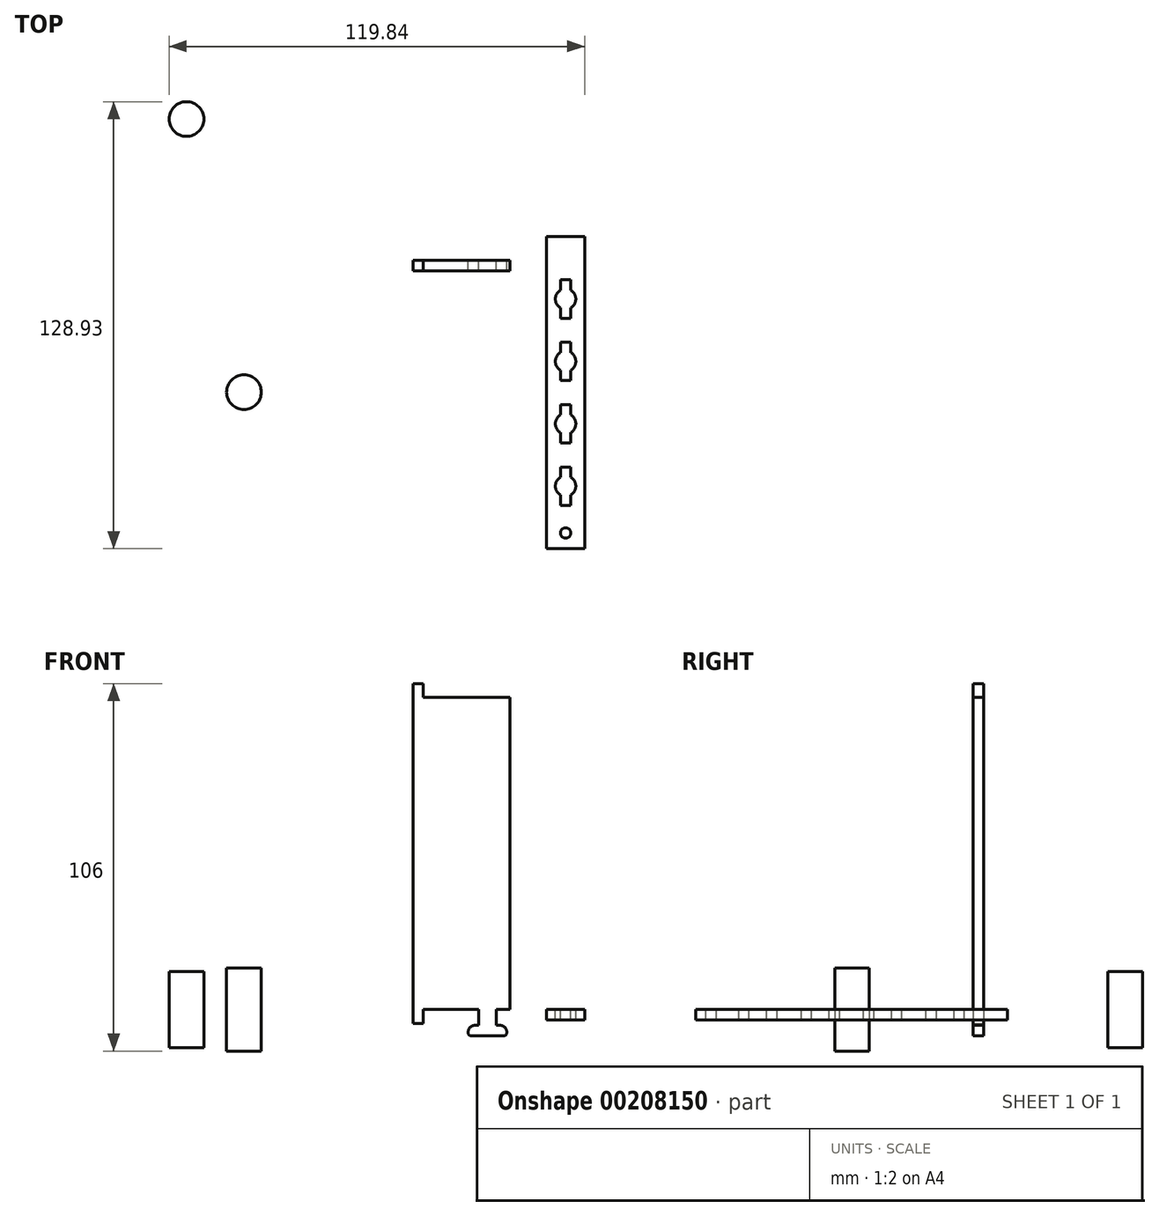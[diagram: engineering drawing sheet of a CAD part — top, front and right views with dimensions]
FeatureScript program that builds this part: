
annotation { "Feature Type Name" : "Feature", "Feature Type Description" : "" }
export const myFeature = defineFeature(function(context is Context, id is Id, definition is map)
    precondition{}
    {
        {
            var Q0;
            Q0=qCreatedBy(makeId("Front.planeOp"),FACE);
            var sketch = newSketch(context, id + "F0", { "sketchPlane" : qUnion([Q0])});
            skLineSegment(sketch, "E0.left", {"start": v(0, 0) * mm, "end": v(0, 90) * mm});
            skLineSegment(sketch, "E1.top", {"start": v(0, -4) * mm, "end": v(3, -4) * mm});
            skLineSegment(sketch, "E1.left", {"start": v(0, 0) * mm, "end": v(0, -4) * mm});
            skLineSegment(sketch, "E1.right", {"start": v(3, 0) * mm, "end": v(3, -4) * mm});
            skLineSegment(sketch, "E2.left", {"start": v(19, 0) * mm, "end": v(19, -4.6) * mm});
            skLineSegment(sketch, "E2.right", {"start": v(24, 0) * mm, "end": v(24, -4.6) * mm});
            skLineSegment(sketch, "E3.top", {"start": v(0, 94) * mm, "end": v(3, 94) * mm});
            skLineSegment(sketch, "E3.left", {"start": v(0, 90) * mm, "end": v(0, 94) * mm});
            skLineSegment(sketch, "E3.right", {"start": v(3, 90) * mm, "end": v(3, 94) * mm});
            skLineSegment(sketch, "E4", {"start": v(28, 0) * mm, "end": v(24, 0) * mm});
            skLineSegment(sketch, "E5", {"start": v(19, 0) * mm, "end": v(3, 0) * mm});
            skLineSegment(sketch, "E6", {"start": v(3, 90) * mm, "end": v(7, 90) * mm});
            skLineSegment(sketch, "E7", {"start": v(19, -4.6) * mm, "end": v(17.76, -4.6) * mm});
            skLineSegment(sketch, "E8", {"start": v(15.96, -6.4) * mm, "end": v(15.96, -6.8) * mm});
            skLineSegment(sketch, "E9", {"start": v(16.76, -7.6) * mm, "end": v(26.24, -7.6) * mm});
            skLineSegment(sketch, "E10", {"start": v(27.04, -6.8) * mm, "end": v(27.04, -6.4) * mm});
            skLineSegment(sketch, "E11", {"start": v(25.24, -4.6) * mm, "end": v(24, -4.6) * mm});
            skPoint(sketch, "E12.visualSharp", {"position": v(15.96, -4.6) * mm});
            skArc(sketch, "E12.filletArc", {"start": v(17.76, -4.6) * mm, "mid": v(16.49, -5.13) * mm, "end": v(15.96, -6.4) * mm});
            skPoint(sketch, "E13.visualSharp", {"position": v(27.04, -4.6) * mm});
            skArc(sketch, "E13.filletArc", {"start": v(27.04, -6.4) * mm, "mid": v(26.51, -5.13) * mm, "end": v(25.24, -4.6) * mm});
            skPoint(sketch, "E14.visualSharp", {"position": v(15.96, -7.6) * mm});
            skArc(sketch, "E14.filletArc", {"start": v(15.96, -6.8) * mm, "mid": v(16.2, -7.37) * mm, "end": v(16.76, -7.6) * mm});
            skPoint(sketch, "E15.visualSharp", {"position": v(27.04, -7.6) * mm});
            skArc(sketch, "E15.filletArc", {"start": v(26.24, -7.6) * mm, "mid": v(26.8, -7.37) * mm, "end": v(27.04, -6.8) * mm});
            skLineSegment(sketch, "E16", {"start": v(7, 90) * mm, "end": v(28, 90) * mm});
            skLineSegment(sketch, "E17", {"start": v(28, 0) * mm, "end": v(28, 90) * mm});
            skSolve(sketch);
        }
        {
            var Q0;
            Q0=qCreatedBy(makeId("Top.planeOp"),FACE);
            var sketch = newSketch(context, id + "F1", { "sketchPlane" : qUnion([Q0])});
            skLineSegment(sketch, "E18.bottom", {"start": v(38.53, -83.11) * mm, "end": v(49.53, -83.11) * mm});
            skLineSegment(sketch, "E18.top", {"start": v(38.53, 6.89) * mm, "end": v(49.53, 6.89) * mm});
            skLineSegment(sketch, "E18.left", {"start": v(38.53, -83.11) * mm, "end": v(38.53, 6.89) * mm});
            skLineSegment(sketch, "E18.right", {"start": v(49.53, -83.11) * mm, "end": v(49.53, 6.89) * mm});
            skLineSegment(sketch, "E19", {"start": v(44.03, 6.89) * mm, "end": v(44.03, -83.11) * mm, "construction": true});
            skCircle(sketch, "E20", {"center": v(44.03, -11.11) * mm, "radius": 2.95 * mm});
            skLineSegment(sketch, "E21", {"start": v(42.53, -8.57) * mm, "end": v(42.53, -5.57) * mm});
            skLineSegment(sketch, "E22", {"start": v(42.53, -5.57) * mm, "end": v(45.53, -5.57) * mm});
            skLineSegment(sketch, "E23", {"start": v(45.53, -5.57) * mm, "end": v(45.53, -8.57) * mm});
            skLineSegment(sketch, "E24", {"start": v(42.53, -13.65) * mm, "end": v(42.53, -16.65) * mm});
            skLineSegment(sketch, "E25", {"start": v(42.53, -16.65) * mm, "end": v(45.53, -16.65) * mm});
            skLineSegment(sketch, "E26", {"start": v(45.53, -16.65) * mm, "end": v(45.53, -13.65) * mm});
            skCircle(sketch, "E27.0.1.0", {"center": v(44.03, -29.11) * mm, "radius": 2.95 * mm});
            skLineSegment(sketch, "E27.0.1.1", {"start": v(42.53, -23.57) * mm, "end": v(45.53, -23.57) * mm});
            skLineSegment(sketch, "E27.0.1.2", {"start": v(42.53, -26.57) * mm, "end": v(42.53, -23.57) * mm});
            skLineSegment(sketch, "E27.0.1.3", {"start": v(45.53, -23.57) * mm, "end": v(45.53, -26.57) * mm});
            skLineSegment(sketch, "E27.0.1.4", {"start": v(42.53, -31.65) * mm, "end": v(42.53, -34.65) * mm});
            skLineSegment(sketch, "E27.0.1.5", {"start": v(45.53, -34.65) * mm, "end": v(45.53, -31.65) * mm});
            skLineSegment(sketch, "E27.0.1.6", {"start": v(42.53, -34.65) * mm, "end": v(45.53, -34.65) * mm});
            skCircle(sketch, "E27.0.2.0", {"center": v(44.03, -47.11) * mm, "radius": 2.95 * mm});
            skLineSegment(sketch, "E27.0.2.1", {"start": v(42.53, -41.57) * mm, "end": v(45.53, -41.57) * mm});
            skLineSegment(sketch, "E27.0.2.2", {"start": v(42.53, -44.57) * mm, "end": v(42.53, -41.57) * mm});
            skLineSegment(sketch, "E27.0.2.3", {"start": v(45.53, -41.57) * mm, "end": v(45.53, -44.57) * mm});
            skLineSegment(sketch, "E27.0.2.4", {"start": v(42.53, -49.65) * mm, "end": v(42.53, -52.65) * mm});
            skLineSegment(sketch, "E27.0.2.5", {"start": v(45.53, -52.65) * mm, "end": v(45.53, -49.65) * mm});
            skLineSegment(sketch, "E27.0.2.6", {"start": v(42.53, -52.65) * mm, "end": v(45.53, -52.65) * mm});
            skCircle(sketch, "E27.0.3.0", {"center": v(44.03, -65.11) * mm, "radius": 2.95 * mm});
            skLineSegment(sketch, "E27.0.3.1", {"start": v(42.53, -59.57) * mm, "end": v(45.53, -59.57) * mm});
            skLineSegment(sketch, "E27.0.3.2", {"start": v(42.53, -62.57) * mm, "end": v(42.53, -59.57) * mm});
            skLineSegment(sketch, "E27.0.3.3", {"start": v(45.53, -59.57) * mm, "end": v(45.53, -62.57) * mm});
            skLineSegment(sketch, "E27.0.3.4", {"start": v(42.53, -67.65) * mm, "end": v(42.53, -70.65) * mm});
            skLineSegment(sketch, "E27.0.3.5", {"start": v(45.53, -70.65) * mm, "end": v(45.53, -67.65) * mm});
            skLineSegment(sketch, "E27.0.3.6", {"start": v(42.53, -70.65) * mm, "end": v(45.53, -70.65) * mm});
            skLineSegment(sketch, "E27.direction1", {"start": v(44.03, -11.11) * mm, "end": v(69.06, -11.11) * mm, "construction": true});
            skLineSegment(sketch, "E27.direction2", {"start": v(44.03, -11.11) * mm, "end": v(44.03, -29.11) * mm, "construction": true});
            skCircle(sketch, "E28", {"center": v(44.03, -78.61) * mm, "radius": 1.5 * mm});
            skSolve(sketch);
        }
        {
            var Q0;
            Q0=makeQuery(id+"F0.imprint","IMPRINT",FACE,{"disambiguationData":[TD([[makeQuery(id+"F0.imprint","IMPRINT",EDGE,{"derivedFrom":sQuery(id+"F0.wireOp",EDGE,"E0.left")}),-1.0]])]});
            extrude(context, id + "F2", {"entities" : qUnion([Q0]), "depth" : 3 * mm});
        }
        {
            var Q0;
            Q0=makeQuery(id+"F1.imprint","IMPRINT",FACE,{"disambiguationData":[TD([[makeQuery(id+"F1.imprint","IMPRINT",EDGE,{"derivedFrom":sQuery(id+"F1.wireOp",EDGE,"E18.bottom")}),1.0]])]});
            extrude(context, id + "F3", {"entities" : qUnion([Q0]), "oppositeDirection" : true, "depth" : 3 * mm});
        }
        {
            var Q0;
            Q0=qCreatedBy(makeId("Top.planeOp"),FACE);
            var sketch = newSketch(context, id + "F4", { "sketchPlane" : qUnion([Q0])});
            skCircle(sketch, "E29", {"center": v(-65.31, 40.82) * mm, "radius": 5 * mm});
            skSolve(sketch);
        }
        {
            var Q0;
            Q0=makeQuery(id+"F4.imprint","IMPRINT",FACE,{"disambiguationData":[TD([[makeQuery(id+"F4.imprint","IMPRINT",EDGE,{"derivedFrom":sQuery(id+"F4.wireOp",EDGE,"E29")}),1.0]])]});
            extrude(context, id + "F5", {"entities" : qUnion([Q0]), "endBound" : BoundingType.SYMMETRIC, "depth" : 22 * mm});
        }
        {
            var Q0;
            Q0=qCreatedBy(makeId("Top.planeOp"),FACE);
            var sketch = newSketch(context, id + "F6", { "sketchPlane" : qUnion([Q0])});
            skCircle(sketch, "E30", {"center": v(-48.74, -37.98) * mm, "radius": 5 * mm});
            skSolve(sketch);
        }
        {
            var Q0;
            Q0=makeQuery(id+"F6.imprint","IMPRINT",FACE,{"disambiguationData":[TD([[makeQuery(id+"F6.imprint","IMPRINT",EDGE,{"derivedFrom":sQuery(id+"F6.wireOp",EDGE,"E30")}),1.0]])]});
            extrude(context, id + "F7", {"entities" : qUnion([Q0]), "endBound" : BoundingType.SYMMETRIC, "depth" : 24 * mm});
        }
        {
            var Q0;
            Q0=makeQuery(id+"F2.opExtrude","SWEPT_FACE",FACE,{"disambiguationData":[OSD([sQuery(id+"F0.wireOp",EDGE,"E0.left"),sQuery(id+"F0.wireOp",EDGE,"E1.left"),sQuery(id+"F0.wireOp",EDGE,"E3.left")])]});
            var sketch = newSketch(context, id + "F8", { "sketchPlane" : qUnion([Q0])});
            skLineSegment(sketch, "E31", {"start": v(3, 90) * mm, "end": v(0, 90) * mm});
            skLineSegment(sketch, "E32", {"start": v(0, 0) * mm, "end": v(3, 0) * mm});
            skLineSegment(sketch, "E33", {"start": v(0, 0) * mm, "end": v(0, 90) * mm});
            skLineSegment(sketch, "E34", {"start": v(3, 90) * mm, "end": v(3, 0) * mm});
            skLineSegment(sketch, "E35.bottom", {"start": v(0, 90) * mm, "end": v(3, 90) * mm});
            skLineSegment(sketch, "E35.top", {"start": v(0, 94) * mm, "end": v(3, 94) * mm});
            skLineSegment(sketch, "E35.left", {"start": v(0, 90) * mm, "end": v(0, 94) * mm});
            skLineSegment(sketch, "E35.right", {"start": v(3, 90) * mm, "end": v(3, 94) * mm});
            skLineSegment(sketch, "E36.top", {"start": v(0, -4) * mm, "end": v(3, -4) * mm});
            skLineSegment(sketch, "E36.left", {"start": v(0, 0) * mm, "end": v(0, -4) * mm});
            skLineSegment(sketch, "E36.right", {"start": v(3, 0) * mm, "end": v(3, -4) * mm});
            skSolve(sketch);
        }
        {
            var Q0;
            Q0=makeQuery(id+"F8.imprint","IMPRINT",FACE,{"disambiguationData":[TD([[makeQuery(id+"F8.imprint","IMPRINT",EDGE,{"derivedFrom":sQuery(id+"F8.wireOp",EDGE,"E32")}),-1.0]])]});
            var Q1;
            Q1=makeQuery(id+"F8.imprint","IMPRINT",FACE,{"disambiguationData":[TD([[makeQuery(id+"F8.imprint","IMPRINT",EDGE,{"derivedFrom":sQuery(id+"F8.wireOp",EDGE,"E35.bottom")}),1.0]])]});
            var Q2;
            Q2=makeQuery(id+"F2.opExtrude","SWEPT_BODY",BODY,{"disambiguationData":[OSD([sQuery(id+"F0.wireOp",EDGE,"E0.left"),sQuery(id+"F0.wireOp",EDGE,"E1.top"),sQuery(id+"F0.wireOp",EDGE,"E1.left"),sQuery(id+"F0.wireOp",EDGE,"E1.right"),sQuery(id+"F0.wireOp",EDGE,"E2.left"),sQuery(id+"F0.wireOp",EDGE,"E2.right"),sQuery(id+"F0.wireOp",EDGE,"E3.top"),sQuery(id+"F0.wireOp",EDGE,"E3.left"),sQuery(id+"F0.wireOp",EDGE,"E3.right"),sQuery(id+"F0.wireOp",EDGE,"E4"),sQuery(id+"F0.wireOp",EDGE,"E5"),sQuery(id+"F0.wireOp",EDGE,"E6"),sQuery(id+"F0.wireOp",EDGE,"E7"),sQuery(id+"F0.wireOp",EDGE,"E8"),sQuery(id+"F0.wireOp",EDGE,"E9"),sQuery(id+"F0.wireOp",EDGE,"E10"),sQuery(id+"F0.wireOp",EDGE,"E11"),sQuery(id+"F0.wireOp",EDGE,"E12.filletArc"),sQuery(id+"F0.wireOp",EDGE,"E13.filletArc"),sQuery(id+"F0.wireOp",EDGE,"E14.filletArc"),sQuery(id+"F0.wireOp",EDGE,"E15.filletArc"),sQuery(id+"F0.wireOp",EDGE,"E16"),sQuery(id+"F0.wireOp",EDGE,"E17")])]});
            extrude(context, id + "F9", {"entities" : qUnion([Q0, Q1]), "operationType" : NewBodyOperationType.ADD, "endBound" : BoundingType.UP_TO_BODY, "oppositeDirection" : true, "endBoundEntityBody" : qUnion([Q2]), "depth" : 25 * mm});
        }
    });
